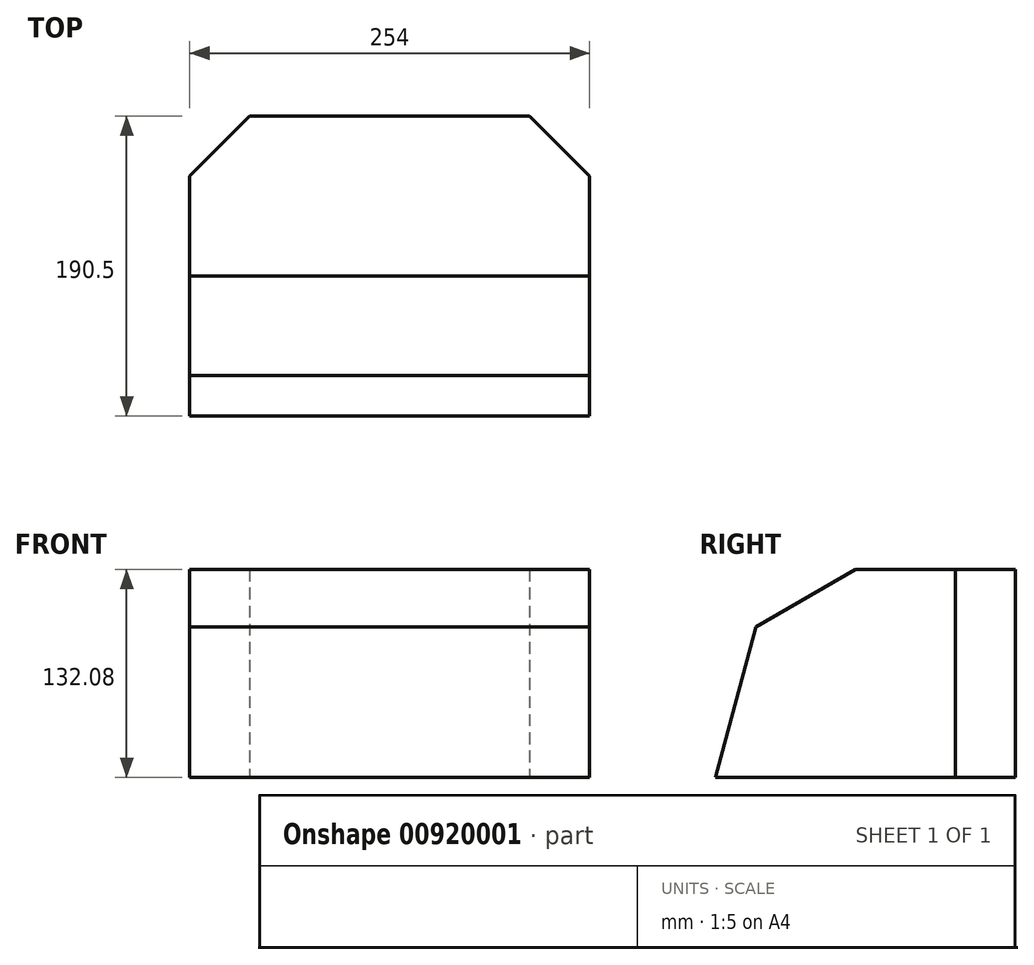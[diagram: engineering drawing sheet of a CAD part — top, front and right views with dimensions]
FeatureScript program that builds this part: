
annotation { "Feature Type Name" : "Feature", "Feature Type Description" : "" }
export const myFeature = defineFeature(function(context is Context, id is Id, definition is map)
    precondition{}
    {
        {
            var Q0;
            Q0=qCreatedBy(makeId("Top.planeOp"),FACE);
            var sketch = newSketch(context, id + "F0", { "sketchPlane" : qUnion([Q0])});
            skLineSegment(sketch, "E0.bottom", {"start": v(-127, 76.2) * mm, "end": v(127, 76.2) * mm, "construction": true});
            skLineSegment(sketch, "E0.top", {"start": v(-127, -76.2) * mm, "end": v(127, -76.2) * mm});
            skLineSegment(sketch, "E0.left", {"start": v(-127, 76.2) * mm, "end": v(-127, -76.2) * mm});
            skLineSegment(sketch, "E0.right", {"start": v(127, 76.2) * mm, "end": v(127, -76.2) * mm});
            skLineSegment(sketch, "E1", {"start": v(-127, 76.2) * mm, "end": v(-88.9, 114.3) * mm});
            skLineSegment(sketch, "E2", {"start": v(-88.9, 114.3) * mm, "end": v(88.9, 114.3) * mm});
            skLineSegment(sketch, "E3", {"start": v(88.9, 114.3) * mm, "end": v(127, 76.2) * mm});
            skPoint(sketch, "E4", {"position": v(0, 114.3) * mm});
            skLineSegment(sketch, "E5", {"start": v(-127, 76.2) * mm, "end": v(127, -76.2) * mm, "construction": true});
            skPoint(sketch, "E6", {"position": v(0, 0) * mm});
            skSolve(sketch);
        }
        {
            var Q0;
            Q0 = qSketchRegion(id + "F0", true);
            extrude(context, id + "F1", {"entities" : qUnion([Q0]), "depth" : 132.08 * mm, "offsetDistance" : 25.4 * mm});
        }
        {
            var Q0;
            Q0=makeQuery(id+"F1.opExtrude","SWEPT_FACE",FACE,{"disambiguationData":[OSD([sQuery(id+"F0.wireOp",EDGE,"E0.right")])]});
            var sketch = newSketch(context, id + "F2", { "sketchPlane" : qUnion([Q0])});
            skLineSegment(sketch, "E7", {"start": v(-76.2, 0) * mm, "end": v(-40.8, 132.08) * mm});
            skLineSegment(sketch, "E8", {"start": v(-40.8, 132.08) * mm, "end": v(-76.2, 132.08) * mm});
            skLineSegment(sketch, "E9", {"start": v(-76.2, 132.08) * mm, "end": v(-76.2, 0) * mm});
            skSolve(sketch);
        }
        {
            var Q0;
            Q0 = qSketchRegion(id + "F2", true);
            extrude(context, id + "F3", {"entities" : qUnion([Q0]), "operationType" : NewBodyOperationType.REMOVE, "endBound" : BoundingType.THROUGH_ALL, "oppositeDirection" : true, "depth" : 25.4 * mm, "offsetDistance" : 25.4 * mm});
        }
        {
            var Q0;
            Q0=makeQuery(id+"F1.opExtrude","SWEPT_FACE",FACE,{"disambiguationData":[OSD([sQuery(id+"F0.wireOp",EDGE,"E0.right")])]});
            var sketch = newSketch(context, id + "F4", { "sketchPlane" : qUnion([Q0])});
            skLineSegment(sketch, "E10", {"start": v(-76.2, 132.08) * mm, "end": v(-76.2, 80.75) * mm});
            skLineSegment(sketch, "E11", {"start": v(-76.2, 132.08) * mm, "end": v(12.7, 132.08) * mm});
            skLineSegment(sketch, "E12", {"start": v(12.7, 132.08) * mm, "end": v(-76.2, 80.75) * mm});
            skSolve(sketch);
        }
        {
            var Q0;
            Q0 = qSketchRegion(id + "F4", true);
            extrude(context, id + "F5", {"entities" : qUnion([Q0]), "operationType" : NewBodyOperationType.REMOVE, "endBound" : BoundingType.THROUGH_ALL, "oppositeDirection" : true, "depth" : 25.4 * mm, "offsetDistance" : 25.4 * mm});
        }
    });
